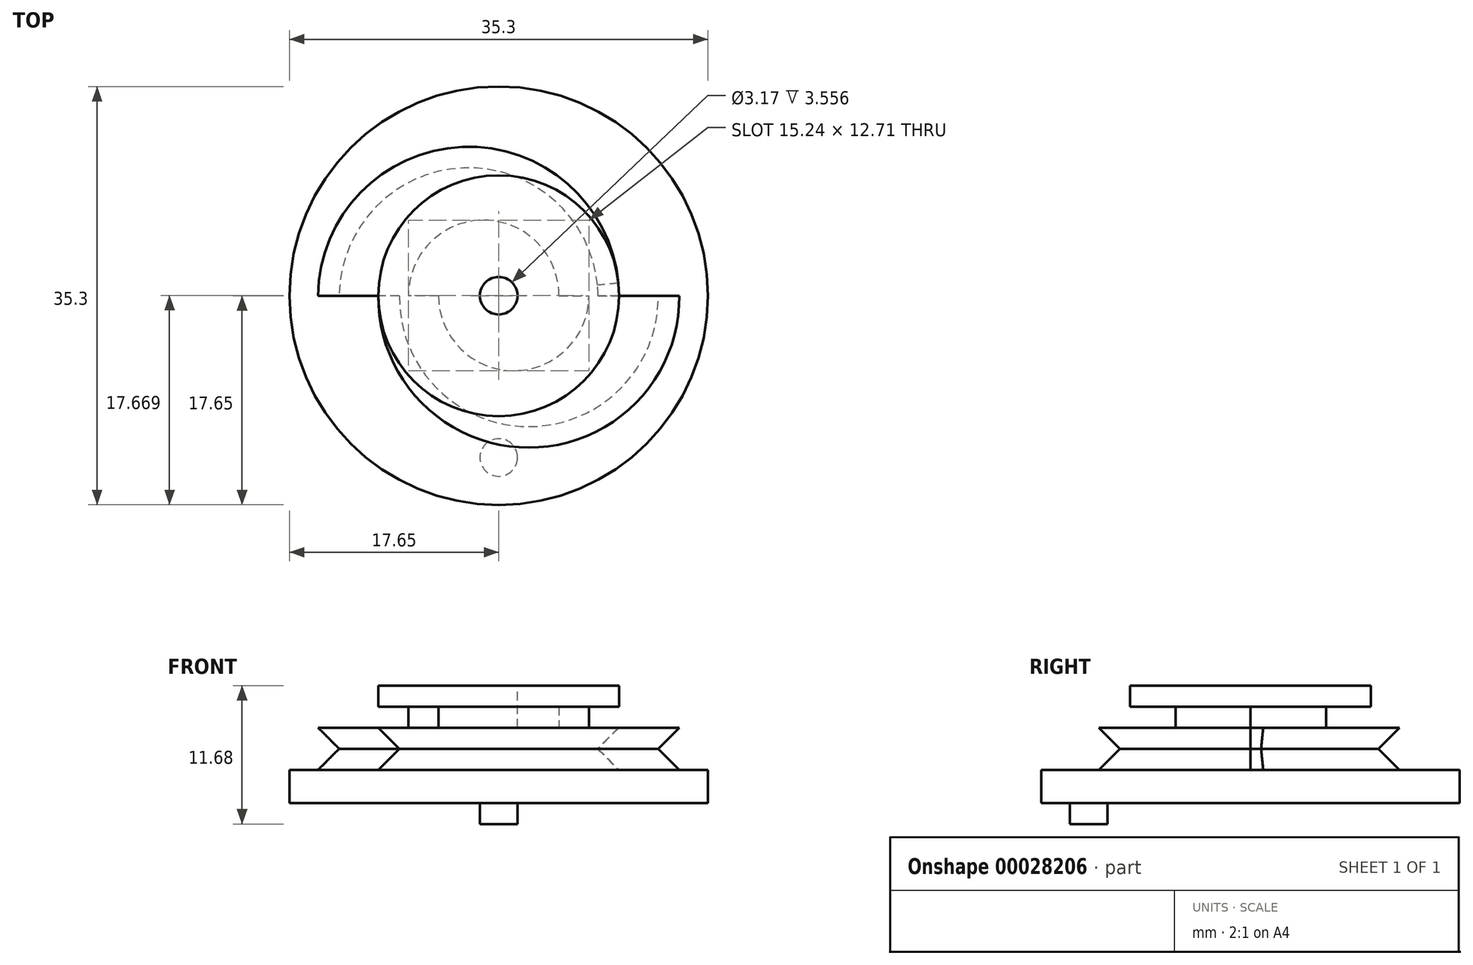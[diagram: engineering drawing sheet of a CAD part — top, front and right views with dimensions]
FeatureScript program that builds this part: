
annotation { "Feature Type Name" : "Feature", "Feature Type Description" : "" }
export const myFeature = defineFeature(function(context is Context, id is Id, definition is map)
    precondition{}
    {
        {
            var Q0;
            Q0=qCreatedBy(makeId("Top.planeOp"),FACE);
            var sketch = newSketch(context, id + "F0", { "sketchPlane" : qUnion([Q0])});
            skCircle(sketch, "E0", {"center": v(0, 0) * mm, "radius": 17.65 * mm});
            skSolve(sketch);
        }
        {
            var Q0;
            Q0 = qSketchRegion(id + "F0", true);
            extrude(context, id + "F1", {"entities" : qUnion([Q0]), "oppositeDirection" : true, "depth" : 2.8 * mm});
        }
        {
            var Q0;
            Q0=makeQuery(id+"F1.opExtrude","CAP_FACE",FACE,{"disambiguationData":[OSD([sQuery(id+"F0.wireOp",EDGE,"E0")])],"isStart":false});
            var sketch = newSketch(context, id + "F2", { "sketchPlane" : qUnion([Q0])});
            skCircle(sketch, "E1", {"center": v(0, 13.65) * mm, "radius": 1.59 * mm});
            skSolve(sketch);
        }
        {
            var Q0;
            Q0 = qSketchRegion(id + "F2", true);
            extrude(context, id + "F3", {"entities" : qUnion([Q0]), "operationType" : NewBodyOperationType.ADD, "depth" : 1.78 * mm});
        }
        {
            var Q0;
            Q0=makeQuery(id+"F1.opExtrude","CAP_FACE",FACE,{"disambiguationData":[OSD([sQuery(id+"F0.wireOp",EDGE,"E0")])],"isStart":true});
            var sketch = newSketch(context, id + "F4", { "sketchPlane" : qUnion([Q0])});
            skCircle(sketch, "E2", {"center": v(0, 0) * mm, "radius": 10.16 * mm});
            skLineSegment(sketch, "E3", {"start": v(-10.16, 0) * mm, "end": v(-15.24, 0) * mm});
            skLineSegment(sketch, "E4", {"start": v(10.16, 0) * mm, "end": v(15.24, 0) * mm});
            skArc(sketch, "E5", {"start": v(-10.16, 0) * mm, "mid": v(2.54, -12.82) * mm, "end": v(15.24, 0) * mm});
            skArc(sketch, "E6", {"start": v(10.16, 0) * mm, "mid": v(-2.54, 12.57) * mm, "end": v(-15.24, 0) * mm});
            skSolve(sketch);
        }
        {
            var Q0;
            Q0 = qSketchRegion(id + "F4", true);
            extrude(context, id + "F5", {"entities" : qUnion([Q0]), "operationType" : NewBodyOperationType.ADD, "depth" : 1.78 * mm});
        }
        {
            var Q0;
            Q0=makeQuery(id+"F5.opExtrude","CAP_FACE",FACE,{"disambiguationData":[OSD([sQuery(id+"F4.wireOp",EDGE,"E2"),sQuery(id+"F4.wireOp",EDGE,"E3"),sQuery(id+"F4.wireOp",EDGE,"E4"),sQuery(id+"F4.wireOp",EDGE,"E5"),sQuery(id+"F4.wireOp",EDGE,"E6")])],"isStart":false});
            extrude(context, id + "F6", {"entities" : qUnion([Q0]), "depth" : 1.78 * mm});
        }
        {
            var Q0;
            Q0=makeQuery(id+"F5.opExtrude","CAP_EDGE",EDGE,{"disambiguationData":[OSD([sQuery(id+"F4.wireOp",EDGE,"E5")])],"isStart":false});
            var Q1;
            Q1=makeQuery(id+"F5.opExtrude","CAP_EDGE",EDGE,{"disambiguationData":[OSD([sQuery(id+"F4.wireOp",EDGE,"E6")])],"isStart":false});
            var Q2;
            Q2=makeQuery(id+"F5.opExtrude","CAP_EDGE",EDGE,{"disambiguationData":[OSD([sQuery(id+"F4.wireOp",EDGE,"E2")])],"isStart":false});
            chamfer(context, id + "F7", {"entities" : qUnion([Q0, Q1, Q2]), "chamferType" : ChamferType.TWO_OFFSETS, "width1" : 1.78 * mm, "oppositeDirection" : false, "width2" : 1.78 * mm, "tangentPropagation" : true});
        }
        {
            var Q0;
            Q0=makeQuery(id+"F6.opExtrude","CAP_EDGE",EDGE,{"disambiguationData":[OSD([sQuery(id+"F4.wireOp",EDGE,"E5")])],"isStart":true});
            var Q1;
            Q1=makeQuery(id+"F6.opExtrude","CAP_EDGE",EDGE,{"disambiguationData":[OSD([sQuery(id+"F4.wireOp",EDGE,"E6")])],"isStart":true});
            var Q2;
            Q2=makeQuery(id+"F6.opExtrude","CAP_EDGE",EDGE,{"disambiguationData":[OSD([sQuery(id+"F4.wireOp",EDGE,"E2")])],"isStart":true});
            chamfer(context, id + "F8", {"entities" : qUnion([Q0, Q1, Q2]), "chamferType" : ChamferType.TWO_OFFSETS, "width1" : 1.78 * mm, "oppositeDirection" : false, "width2" : 1.78 * mm, "tangentPropagation" : true});
        }
        {
            var Q0;
            Q0=makeQuery(id+"F6.opExtrude","CAP_FACE",FACE,{"disambiguationData":[OSD([sQuery(id+"F4.wireOp",EDGE,"E2"),sQuery(id+"F4.wireOp",EDGE,"E3"),sQuery(id+"F4.wireOp",EDGE,"E4"),sQuery(id+"F4.wireOp",EDGE,"E5"),sQuery(id+"F4.wireOp",EDGE,"E6")])],"isStart":false});
            var sketch = newSketch(context, id + "F9", { "sketchPlane" : qUnion([Q0])});
            skCircle(sketch, "E7", {"center": v(0, 0) * mm, "radius": 5.08 * mm});
            skLineSegment(sketch, "E8", {"start": v(5.08, 0) * mm, "end": v(7.62, 0) * mm});
            skLineSegment(sketch, "E9", {"start": v(-5.08, 0) * mm, "end": v(-7.62, 0) * mm});
            skArc(sketch, "E10", {"start": v(-5.08, 0) * mm, "mid": v(1.27, -6.33) * mm, "end": v(7.62, 0) * mm});
            skArc(sketch, "E11", {"start": v(5.08, 0) * mm, "mid": v(-1.27, 6.37) * mm, "end": v(-7.62, 0) * mm});
            skSolve(sketch);
        }
        {
            var Q0;
            {var subQ1=sQuery(id+"F9.wireOp",EDGE,"E9");Q0=makeQuery(id+"F9.imprint","IMPRINT",FACE,{"disambiguationData":[TD([[makeQuery(id+"F9.imprint","IMPRINT",EDGE,{"derivedFrom":subQ1}),-1.0]])]});}
            var Q1;
            {var subQ0=sQuery(id+"F9.wireOp",EDGE,"E10");var subQ1=sQuery(id+"F9.wireOp",EDGE,"E7");var subQ2=makeQuery(id+"F9.imprint","INTERSECT",VERTEX,{"derivedFrom":[subQ1,subQ0]});Q1=makeQuery(id+"F9.imprint","IMPRINT",FACE,{"disambiguationData":[TD([[makeQuery(id+"F9.imprint","IMPRINT",EDGE,{"disambiguationData":[TD([[subQ2,-1.0]])],"derivedFrom":subQ1}),1.0]])]});}
            var Q2;
            {var subQ3=sQuery(id+"F9.wireOp",EDGE,"E8");Q2=makeQuery(id+"F9.imprint","IMPRINT",FACE,{"disambiguationData":[TD([[makeQuery(id+"F9.imprint","IMPRINT",EDGE,{"derivedFrom":subQ3}),-1.0]])]});}
            extrude(context, id + "F10", {"entities" : qUnion([Q0, Q1, Q2]), "operationType" : NewBodyOperationType.ADD, "depth" : 1.78 * mm});
        }
        {
            var Q0;
            Q0=makeQuery(id+"F10.opExtrude","CAP_FACE",FACE,{"disambiguationData":[OSD([sQuery(id+"F9.wireOp",EDGE,"E8"),sQuery(id+"F9.wireOp",EDGE,"E9"),sQuery(id+"F9.wireOp",EDGE,"E10"),sQuery(id+"F9.wireOp",EDGE,"E11")])],"isStart":false});
            var sketch = newSketch(context, id + "F11", { "sketchPlane" : qUnion([Q0])});
            skCircle(sketch, "E12", {"center": v(0, 0) * mm, "radius": 10.16 * mm});
            skSolve(sketch);
        }
        {
            var Q0;
            Q0 = qSketchRegion(id + "F11", true);
            extrude(context, id + "F12", {"entities" : qUnion([Q0]), "operationType" : NewBodyOperationType.ADD, "depth" : 1.78 * mm});
        }
        {
            var Q0;
            Q0=makeQuery(id+"F12.opExtrude","CAP_FACE",FACE,{"disambiguationData":[OSD([sQuery(id+"F11.wireOp",EDGE,"E12")])],"isStart":false});
            var sketch = newSketch(context, id + "F13", { "sketchPlane" : qUnion([Q0])});
            skCircle(sketch, "E13", {"center": v(0, 0) * mm, "radius": 1.59 * mm});
            skSolve(sketch);
        }
        {
            var Q0;
            Q0 = qSketchRegion(id + "F13", true);
            extrude(context, id + "F14", {"entities" : qUnion([Q0]), "operationType" : NewBodyOperationType.REMOVE, "oppositeDirection" : true, "depth" : 3.56 * mm});
        }
    });
